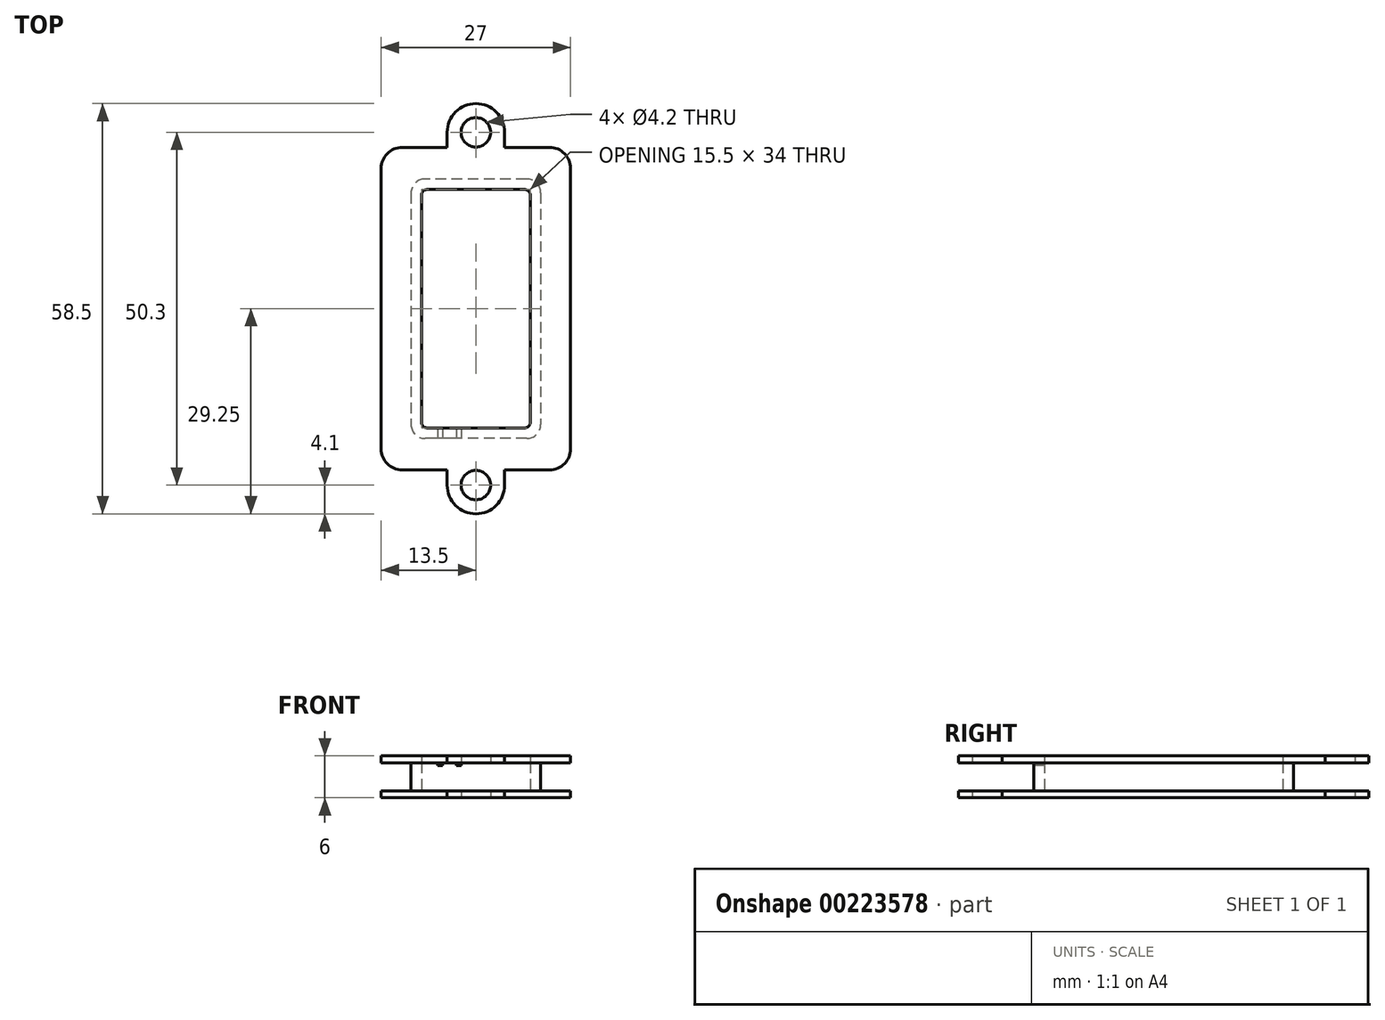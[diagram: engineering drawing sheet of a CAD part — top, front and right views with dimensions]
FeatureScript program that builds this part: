
annotation { "Feature Type Name" : "Feature", "Feature Type Description" : "" }
export const myFeature = defineFeature(function(context is Context, id is Id, definition is map)
    precondition{}
    {
        {
            var Q0;
            Q0=qCreatedBy(makeId("Top.planeOp"),FACE);
            var sketch = newSketch(context, id + "F0", { "sketchPlane" : qUnion([Q0])});
            skLineSegment(sketch, "E0.bottom", {"start": v(10.5, 23) * mm, "end": v(4.1, 23) * mm});
            skLineSegment(sketch, "E0.top", {"start": v(10.5, -23) * mm, "end": v(4.1, -23) * mm});
            skLineSegment(sketch, "E0.left", {"start": v(13.5, 20) * mm, "end": v(13.5, -20) * mm});
            skLineSegment(sketch, "E0.right", {"start": v(-13.5, 20) * mm, "end": v(-13.5, -20) * mm});
            skPoint(sketch, "E0.middle", {"position": v(0, 0) * mm});
            skPoint(sketch, "E1.visualSharp", {"position": v(-13.5, 23) * mm});
            skArc(sketch, "E1.filletArc", {"start": v(-10.5, 23) * mm, "mid": v(-12.62, 22.12) * mm, "end": v(-13.5, 20) * mm});
            skPoint(sketch, "E2.visualSharp", {"position": v(13.5, 23) * mm});
            skArc(sketch, "E2.filletArc", {"start": v(13.5, 20) * mm, "mid": v(12.62, 22.12) * mm, "end": v(10.5, 23) * mm});
            skPoint(sketch, "E3.visualSharp", {"position": v(13.5, -23) * mm});
            skArc(sketch, "E3.filletArc", {"start": v(10.5, -23) * mm, "mid": v(12.62, -22.12) * mm, "end": v(13.5, -20) * mm});
            skPoint(sketch, "E4.visualSharp", {"position": v(-13.5, -23) * mm});
            skArc(sketch, "E4.filletArc", {"start": v(-13.5, -20) * mm, "mid": v(-12.62, -22.12) * mm, "end": v(-10.5, -23) * mm});
            skCircle(sketch, "E5", {"center": v(0, 25.15) * mm, "radius": 2.1 * mm});
            skCircle(sketch, "E6", {"center": v(0, -25.15) * mm, "radius": 2.1 * mm});
            skArc(sketch, "E7", {"start": v(4.1, 25.15) * mm, "mid": v(0, 29.25) * mm, "end": v(-4.1, 25.15) * mm});
            skLineSegment(sketch, "E8", {"start": v(-4.1, 25.15) * mm, "end": v(-4.1, 23) * mm});
            skLineSegment(sketch, "E9", {"start": v(4.1, 25.15) * mm, "end": v(4.1, 23) * mm});
            skLineSegment(sketch, "E10.MirrorCS", {"start": v(-4.1, -25.15) * mm, "end": v(-4.1, -23) * mm});
            skArc(sketch, "E11.MirrorCS", {"start": v(4.1, -25.15) * mm, "mid": v(0, -29.25) * mm, "end": v(-4.1, -25.15) * mm});
            skLineSegment(sketch, "E12.MirrorCS", {"start": v(4.1, -25.15) * mm, "end": v(4.1, -23) * mm});
            skLineSegment(sketch, "E13.trimOffspring", {"start": v(-4.1, 23) * mm, "end": v(-10.5, 23) * mm});
            skLineSegment(sketch, "E14.trimOffspring", {"start": v(-4.1, -23) * mm, "end": v(-10.5, -23) * mm});
            skSolve(sketch);
        }
        {
            var Q0;
            Q0 = qSketchRegion(id + "F0", true);
            extrude(context, id + "F1", {"entities" : qUnion([Q0]), "depth" : 1 * mm});
        }
        {
            var Q0;
            Q0=makeQuery(id+"F1.opExtrude","CAP_FACE",FACE,{"disambiguationData":[OSD([sQuery(id+"F0.wireOp",EDGE,"E0.bottom"),sQuery(id+"F0.wireOp",EDGE,"E0.top"),sQuery(id+"F0.wireOp",EDGE,"E0.left"),sQuery(id+"F0.wireOp",EDGE,"E0.right"),sQuery(id+"F0.wireOp",EDGE,"E1.filletArc"),sQuery(id+"F0.wireOp",EDGE,"E2.filletArc"),sQuery(id+"F0.wireOp",EDGE,"E3.filletArc"),sQuery(id+"F0.wireOp",EDGE,"E4.filletArc"),sQuery(id+"F0.wireOp",EDGE,"E5"),sQuery(id+"F0.wireOp",EDGE,"E6"),sQuery(id+"F0.wireOp",EDGE,"E7"),sQuery(id+"F0.wireOp",EDGE,"E8"),sQuery(id+"F0.wireOp",EDGE,"E9"),sQuery(id+"F0.wireOp",EDGE,"E10.MirrorCS"),sQuery(id+"F0.wireOp",EDGE,"E11.MirrorCS"),sQuery(id+"F0.wireOp",EDGE,"E12.MirrorCS"),sQuery(id+"F0.wireOp",EDGE,"E13.trimOffspring"),sQuery(id+"F0.wireOp",EDGE,"E14.trimOffspring")])],"isStart":false});
            var sketch = newSketch(context, id + "F2", { "sketchPlane" : qUnion([Q0])});
            skLineSegment(sketch, "E15.bottom", {"start": v(6.95, 17) * mm, "end": v(-6.95, 17) * mm});
            skLineSegment(sketch, "E15.top", {"start": v(6.95, -17) * mm, "end": v(-6.95, -17) * mm});
            skLineSegment(sketch, "E15.left", {"start": v(7.75, 16.2) * mm, "end": v(7.75, -16.2) * mm});
            skLineSegment(sketch, "E15.right", {"start": v(-7.75, 16.2) * mm, "end": v(-7.75, -16.2) * mm});
            skPoint(sketch, "E15.middle", {"position": v(0, 0) * mm});
            skLineSegment(sketch, "E16.0", {"start": v(-9.25, 16.5) * mm, "end": v(-9.25, -16.5) * mm});
            skLineSegment(sketch, "E16.1", {"start": v(7.25, 18.5) * mm, "end": v(-7.25, 18.5) * mm});
            skLineSegment(sketch, "E16.2", {"start": v(9.25, 16.5) * mm, "end": v(9.25, -16.5) * mm});
            skLineSegment(sketch, "E16.3", {"start": v(7.25, -18.5) * mm, "end": v(-7.25, -18.5) * mm});
            skPoint(sketch, "E17.visualSharp", {"position": v(-9.25, 18.5) * mm});
            skArc(sketch, "E17.filletArc", {"start": v(-7.25, 18.5) * mm, "mid": v(-8.66, 17.91) * mm, "end": v(-9.25, 16.5) * mm});
            skPoint(sketch, "E18.visualSharp", {"position": v(9.25, 18.5) * mm});
            skArc(sketch, "E18.filletArc", {"start": v(9.25, 16.5) * mm, "mid": v(8.66, 17.91) * mm, "end": v(7.25, 18.5) * mm});
            skPoint(sketch, "E19.visualSharp", {"position": v(9.25, -18.5) * mm});
            skArc(sketch, "E19.filletArc", {"start": v(7.25, -18.5) * mm, "mid": v(8.66, -17.91) * mm, "end": v(9.25, -16.5) * mm});
            skPoint(sketch, "E20.visualSharp", {"position": v(-9.25, -18.5) * mm});
            skArc(sketch, "E20.filletArc", {"start": v(-9.25, -16.5) * mm, "mid": v(-8.66, -17.91) * mm, "end": v(-7.25, -18.5) * mm});
            skPoint(sketch, "E21.visualSharp", {"position": v(-7.75, 17) * mm});
            skArc(sketch, "E21.filletArc", {"start": v(-6.95, 17) * mm, "mid": v(-7.52, 16.77) * mm, "end": v(-7.75, 16.2) * mm});
            skPoint(sketch, "E22.visualSharp", {"position": v(7.75, 17) * mm});
            skArc(sketch, "E22.filletArc", {"start": v(7.75, 16.2) * mm, "mid": v(7.52, 16.77) * mm, "end": v(6.95, 17) * mm});
            skPoint(sketch, "E23.visualSharp", {"position": v(7.75, -17) * mm});
            skArc(sketch, "E23.filletArc", {"start": v(6.95, -17) * mm, "mid": v(7.52, -16.77) * mm, "end": v(7.75, -16.2) * mm});
            skPoint(sketch, "E24.visualSharp", {"position": v(-7.75, -17) * mm});
            skArc(sketch, "E24.filletArc", {"start": v(-7.75, -16.2) * mm, "mid": v(-7.52, -16.77) * mm, "end": v(-6.95, -17) * mm});
            skSolve(sketch);
        }
        {
            var Q0;
            Q0 = qSketchRegion(id + "F2", true);
            extrude(context, id + "F3", {"entities" : qUnion([Q0]), "operationType" : NewBodyOperationType.ADD, "depth" : 4 * mm});
        }
        {
            var Q0;
            Q0=makeQuery(id+"F3.opExtrude","CAP_FACE",FACE,{"disambiguationData":[OSD([sQuery(id+"F2.wireOp",EDGE,"E15.bottom"),sQuery(id+"F2.wireOp",EDGE,"E15.top"),sQuery(id+"F2.wireOp",EDGE,"E15.left"),sQuery(id+"F2.wireOp",EDGE,"E15.right"),sQuery(id+"F2.wireOp",EDGE,"E16.0"),sQuery(id+"F2.wireOp",EDGE,"E16.1"),sQuery(id+"F2.wireOp",EDGE,"E16.2"),sQuery(id+"F2.wireOp",EDGE,"E16.3"),sQuery(id+"F2.wireOp",EDGE,"E17.filletArc"),sQuery(id+"F2.wireOp",EDGE,"E18.filletArc"),sQuery(id+"F2.wireOp",EDGE,"E19.filletArc"),sQuery(id+"F2.wireOp",EDGE,"E20.filletArc"),sQuery(id+"F2.wireOp",EDGE,"E21.filletArc"),sQuery(id+"F2.wireOp",EDGE,"E22.filletArc"),sQuery(id+"F2.wireOp",EDGE,"E23.filletArc"),sQuery(id+"F2.wireOp",EDGE,"E24.filletArc")])],"isStart":false});
            var sketch = newSketch(context, id + "F4", { "sketchPlane" : qUnion([Q0])});
            skLineSegment(sketch, "E25.0", {"start": v(6.95, 17) * mm, "end": v(-6.95, 17) * mm});
            skArc(sketch, "E26.0", {"start": v(-6.95, 17) * mm, "mid": v(-7.52, 16.77) * mm, "end": v(-7.75, 16.2) * mm});
            skLineSegment(sketch, "E27.0", {"start": v(-7.75, 16.2) * mm, "end": v(-7.75, -16.2) * mm});
            skArc(sketch, "E28.0", {"start": v(7.75, 16.2) * mm, "mid": v(7.52, 16.77) * mm, "end": v(6.95, 17) * mm});
            skLineSegment(sketch, "E29.0", {"start": v(7.75, 16.2) * mm, "end": v(7.75, -16.2) * mm});
            skArc(sketch, "E30.0", {"start": v(-7.75, -16.2) * mm, "mid": v(-7.52, -16.77) * mm, "end": v(-6.95, -17) * mm});
            skLineSegment(sketch, "E31.0", {"start": v(6.95, -17) * mm, "end": v(-6.95, -17) * mm});
            skArc(sketch, "E32.0", {"start": v(6.95, -17) * mm, "mid": v(7.52, -16.77) * mm, "end": v(7.75, -16.2) * mm});
            skLineSegment(sketch, "E33.0", {"start": v(-13.5, 20) * mm, "end": v(-13.5, -20) * mm});
            skArc(sketch, "E34.0", {"start": v(-13.5, -20) * mm, "mid": v(-12.62, -22.12) * mm, "end": v(-10.5, -23) * mm});
            skLineSegment(sketch, "E35.0", {"start": v(-4.1, -23) * mm, "end": v(-10.5, -23) * mm});
            skLineSegment(sketch, "E36.0", {"start": v(-4.1, -25.15) * mm, "end": v(-4.1, -23) * mm});
            skArc(sketch, "E37.0", {"start": v(4.1, -25.15) * mm, "mid": v(0, -29.25) * mm, "end": v(-4.1, -25.15) * mm});
            skLineSegment(sketch, "E38.0", {"start": v(4.1, -25.15) * mm, "end": v(4.1, -23) * mm});
            skLineSegment(sketch, "E39.0", {"start": v(10.5, -23) * mm, "end": v(4.1, -23) * mm});
            skArc(sketch, "E40.0", {"start": v(10.5, -23) * mm, "mid": v(12.62, -22.12) * mm, "end": v(13.5, -20) * mm});
            skLineSegment(sketch, "E41.0", {"start": v(13.5, 20) * mm, "end": v(13.5, -20) * mm});
            skArc(sketch, "E42.0", {"start": v(13.5, 20) * mm, "mid": v(12.62, 22.12) * mm, "end": v(10.5, 23) * mm});
            skLineSegment(sketch, "E43.0", {"start": v(10.5, 23) * mm, "end": v(4.1, 23) * mm});
            skLineSegment(sketch, "E44.0", {"start": v(4.1, 25.15) * mm, "end": v(4.1, 23) * mm});
            skArc(sketch, "E45.0", {"start": v(4.1, 25.15) * mm, "mid": v(0, 29.25) * mm, "end": v(-4.1, 25.15) * mm});
            skLineSegment(sketch, "E46.0", {"start": v(-4.1, 25.15) * mm, "end": v(-4.1, 23) * mm});
            skLineSegment(sketch, "E47.0", {"start": v(-4.1, 23) * mm, "end": v(-10.5, 23) * mm});
            skArc(sketch, "E48.0", {"start": v(-10.5, 23) * mm, "mid": v(-12.62, 22.12) * mm, "end": v(-13.5, 20) * mm});
            skCircle(sketch, "E49.0", {"center": v(0, -25.15) * mm, "radius": 2.1 * mm});
            skCircle(sketch, "E50.0", {"center": v(0, 25.15) * mm, "radius": 2.1 * mm});
            skSolve(sketch);
        }
        {
            var Q0;
            Q0 = qSketchRegion(id + "F4", true);
            extrude(context, id + "F5", {"entities" : qUnion([Q0]), "depth" : 1 * mm});
        }
        {
            var Q0;
            Q0=makeQuery(id+"F3.opExtrude","CAP_FACE",FACE,{"disambiguationData":[OSD([sQuery(id+"F2.wireOp",EDGE,"E15.bottom"),sQuery(id+"F2.wireOp",EDGE,"E15.top"),sQuery(id+"F2.wireOp",EDGE,"E15.left"),sQuery(id+"F2.wireOp",EDGE,"E15.right"),sQuery(id+"F2.wireOp",EDGE,"E16.0"),sQuery(id+"F2.wireOp",EDGE,"E16.1"),sQuery(id+"F2.wireOp",EDGE,"E16.2"),sQuery(id+"F2.wireOp",EDGE,"E16.3"),sQuery(id+"F2.wireOp",EDGE,"E17.filletArc"),sQuery(id+"F2.wireOp",EDGE,"E18.filletArc"),sQuery(id+"F2.wireOp",EDGE,"E19.filletArc"),sQuery(id+"F2.wireOp",EDGE,"E20.filletArc"),sQuery(id+"F2.wireOp",EDGE,"E21.filletArc"),sQuery(id+"F2.wireOp",EDGE,"E22.filletArc"),sQuery(id+"F2.wireOp",EDGE,"E23.filletArc"),sQuery(id+"F2.wireOp",EDGE,"E24.filletArc")])],"isStart":false});
            var sketch = newSketch(context, id + "F6", { "sketchPlane" : qUnion([Q0])});
            skLineSegment(sketch, "E51.bottom", {"start": v(-5.45, -17) * mm, "end": v(-4.75, -17) * mm});
            skLineSegment(sketch, "E51.top", {"start": v(-5.45, -18.5) * mm, "end": v(-4.75, -18.5) * mm});
            skLineSegment(sketch, "E51.left", {"start": v(-5.45, -17) * mm, "end": v(-5.45, -18.5) * mm});
            skLineSegment(sketch, "E51.right", {"start": v(-4.75, -17) * mm, "end": v(-4.75, -18.5) * mm});
            skLineSegment(sketch, "E52.bottom", {"start": v(-2.75, -17) * mm, "end": v(-2.05, -17) * mm});
            skLineSegment(sketch, "E52.top", {"start": v(-2.75, -18.5) * mm, "end": v(-2.05, -18.5) * mm});
            skLineSegment(sketch, "E52.left", {"start": v(-2.75, -17) * mm, "end": v(-2.75, -18.5) * mm});
            skLineSegment(sketch, "E52.right", {"start": v(-2.05, -17) * mm, "end": v(-2.05, -18.5) * mm});
            skSolve(sketch);
        }
        {
            var Q0;
            Q0 = qSketchRegion(id + "F6", true);
            extrude(context, id + "F7", {"entities" : qUnion([Q0]), "operationType" : NewBodyOperationType.REMOVE, "oppositeDirection" : true, "depth" : .4 * mm});
        }
    });
